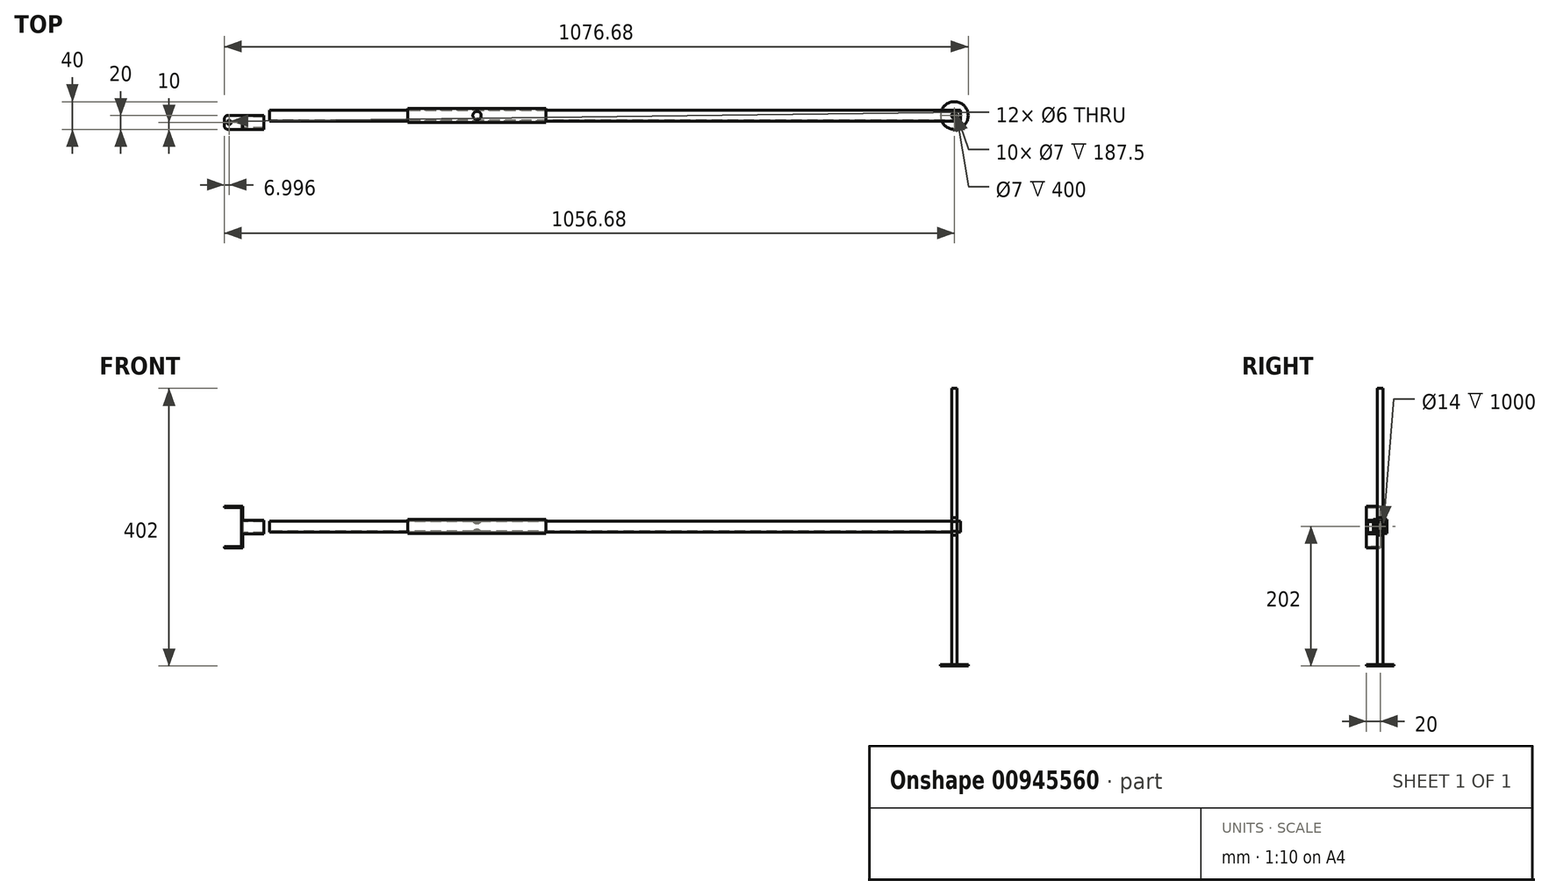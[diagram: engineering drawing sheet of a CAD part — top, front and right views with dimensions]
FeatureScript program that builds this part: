
annotation { "Feature Type Name" : "Feature", "Feature Type Description" : "" }
export const myFeature = defineFeature(function(context is Context, id is Id, definition is map)
    precondition{}
    {
        {
            var Q0;
            Q0=qCreatedBy(makeId("Right.planeOp"),FACE);
            var sketch = newSketch(context, id + "F0", { "sketchPlane" : qUnion([Q0])});
            skLineSegment(sketch, "E0.bottom", {"start": v(10, 10) * mm, "end": v(-10, 10) * mm});
            skLineSegment(sketch, "E0.top", {"start": v(10, -10) * mm, "end": v(-10, -10) * mm});
            skLineSegment(sketch, "E0.left", {"start": v(10, 10) * mm, "end": v(10, -10) * mm});
            skLineSegment(sketch, "E0.right", {"start": v(-10, 10) * mm, "end": v(-10, -10) * mm});
            skPoint(sketch, "E0.middle", {"position": v(0, 0) * mm});
            skLineSegment(sketch, "E1.0", {"start": v(8, 8) * mm, "end": v(-8, 8) * mm});
            skLineSegment(sketch, "E1.1", {"start": v(8, 8) * mm, "end": v(8, -8) * mm});
            skLineSegment(sketch, "E1.2", {"start": v(8, -8) * mm, "end": v(-8, -8) * mm});
            skLineSegment(sketch, "E1.3", {"start": v(-8, 8) * mm, "end": v(-8, -8) * mm});
            skSolve(sketch);
        }
        {
            var Q0;
            Q0=makeQuery(id+"F0.imprint","IMPRINT",FACE,{"disambiguationData":[TD([[makeQuery(id+"F0.imprint","IMPRINT",EDGE,{"derivedFrom":sQuery(id+"F0.wireOp",EDGE,"E0.bottom")}),1.0]])]});
            extrude(context, id + "F1", {"entities" : qUnion([Q0]), "depth" : 200 * mm, "offsetDistance" : 25 * mm});
        }
        {
            var Q0;
            Q0=qCreatedBy(makeId("Right.planeOp"),FACE);
            var sketch = newSketch(context, id + "F2", { "sketchPlane" : qUnion([Q0])});
            skCircle(sketch, "E2", {"center": v(0, 0) * mm, "radius": 8 * mm});
            skCircle(sketch, "E3", {"center": v(0, 0) * mm, "radius": 7 * mm});
            skSolve(sketch);
        }
        {
            var Q0;
            Q0=makeQuery(id+"F2.imprint","IMPRINT",FACE,{"disambiguationData":[TD([[makeQuery(id+"F2.imprint","IMPRINT",EDGE,{"derivedFrom":sQuery(id+"F2.wireOp",EDGE,"E2")}),1.0]])]});
            extrude(context, id + "F3", {"entities" : qUnion([Q0]), "operationType" : NewBodyOperationType.ADD, "depth" : 800 * mm, "offsetDistance" : 25 * mm, "hasSecondDirection" : true, "secondDirectionOppositeDirection" : true, "secondDirectionDepth" : 200 * mm});
        }
        {
            var Q0;
            Q0=makeQuery(id+"F1.opExtrude","SWEPT_FACE",FACE,{"disambiguationData":[OSD([sQuery(id+"F0.wireOp",EDGE,"E0.top")])]});
            var sketch = newSketch(context, id + "F4", { "sketchPlane" : qUnion([Q0])});
            skCircle(sketch, "E4", {"center": v(100, 0) * mm, "radius": 6 * mm});
            skLineSegment(sketch, "E5", {"start": v(0, 0) * mm, "end": v(200, 0) * mm, "construction": true});
            skSolve(sketch);
        }
        {
            var Q0;
            Q0=makeQuery(id+"F4.imprint","IMPRINT",FACE,{"disambiguationData":[TD([[makeQuery(id+"F4.imprint","IMPRINT",EDGE,{"derivedFrom":sQuery(id+"F4.wireOp",EDGE,"E4")}),1.0]])]});
            extrude(context, id + "F5", {"entities" : qUnion([Q0]), "operationType" : NewBodyOperationType.REMOVE, "oppositeDirection" : true, "depth" : 25 * mm, "offsetDistance" : 25 * mm});
        }
        {
            var Q0;
            Q0=qCreatedBy(makeId("Top.planeOp"),FACE);
            var sketch = newSketch(context, id + "F6", { "sketchPlane" : qUnion([Q0])});
            skCircle(sketch, "E6", {"center": v(791, 0) * mm, "radius": 4 * mm});
            skSolve(sketch);
        }
        {
            var Q0;
            Q0 = qSketchRegion(id + "F6", true);
            extrude(context, id + "F7", {"entities" : qUnion([Q0]), "operationType" : NewBodyOperationType.REMOVE, "endBound" : BoundingType.SYMMETRIC, "oppositeDirection" : true, "depth" : 25 * mm, "offsetDistance" : 25 * mm});
        }
        {
            var Q0;
            Q0 = qSketchRegion(id + "F6", true);
            extrude(context, id + "F8", {"entities" : qUnion([Q0]), "endBound" : BoundingType.SYMMETRIC, "depth" : 400 * mm, "offsetDistance" : 25 * mm});
        }
        {
            var Q0;
            Q0=makeQuery(id+"F8.opExtrude","CAP_FACE",FACE,{"disambiguationData":[OSD([sQuery(id+"F6.wireOp",EDGE,"E6")])],"isStart":false});
            var Q1;
            Q1=makeQuery(id+"F8.opExtrude","CAP_FACE",FACE,{"disambiguationData":[OSD([sQuery(id+"F6.wireOp",EDGE,"E6")])],"isStart":true});
            shell(context, id + "F9", {"entities" : qUnion([Q0, Q1]), "thickness" : 0.5 * mm});
        }
        {
            var Q0;
            Q0=makeQuery(id+"F8.opExtrude","CAP_FACE",FACE,{"disambiguationData":[OSD([sQuery(id+"F6.wireOp",EDGE,"E6")])],"isStart":true});
            var sketch = newSketch(context, id + "F10", { "sketchPlane" : qUnion([Q0])});
            skCircle(sketch, "E7", {"center": v(791, 0) * mm, "radius": 20 * mm});
            skSolve(sketch);
        }
        {
            var Q0;
            Q0 = qSketchRegion(id + "F10", true);
            extrude(context, id + "F11", {"entities" : qUnion([Q0]), "depth" : 2 * mm, "offsetDistance" : 25 * mm});
        }
        {
            var Q0;
            Q0=qCreatedBy(makeId("Front.planeOp"),FACE);
            var sketch = newSketch(context, id + "F12", { "sketchPlane" : qUnion([Q0])});
            skLineSegment(sketch, "E8", {"start": v(-208.68, -11) * mm, "end": v(-208.68, 9) * mm});
            skLineSegment(sketch, "E9", {"start": v(-208.68, 9) * mm, "end": v(-238.68, 9) * mm});
            skLineSegment(sketch, "E10", {"start": v(-238.68, 9) * mm, "end": v(-238.68, 29.24) * mm});
            skLineSegment(sketch, "E11", {"start": v(-238.68, 29.24) * mm, "end": v(-265.68, 29.24) * mm});
            skLineSegment(sketch, "E12", {"start": v(-265.68, 29.24) * mm, "end": v(-265.68, 27.24) * mm});
            skLineSegment(sketch, "E13", {"start": v(-265.68, 27.24) * mm, "end": v(-240.68, 27.24) * mm});
            skLineSegment(sketch, "E14", {"start": v(-240.68, 27.24) * mm, "end": v(-240.68, -29.26) * mm});
            skLineSegment(sketch, "E15", {"start": v(-240.68, -29.26) * mm, "end": v(-265.68, -29.26) * mm});
            skLineSegment(sketch, "E16", {"start": v(-265.68, -29.26) * mm, "end": v(-265.68, -31.26) * mm});
            skLineSegment(sketch, "E17", {"start": v(-208.68, -11) * mm, "end": v(-208.68, -11) * mm});
            skLineSegment(sketch, "E18", {"start": v(-208.68, -11) * mm, "end": v(-238.68, -11) * mm});
            skLineSegment(sketch, "E19", {"start": v(-238.68, -11) * mm, "end": v(-238.68, -31.26) * mm});
            skLineSegment(sketch, "E20", {"start": v(-238.68, -31.26) * mm, "end": v(-265.68, -31.26) * mm});
            skSolve(sketch);
        }
        {
            var Q0;
            Q0 = qSketchRegion(id + "F12", true);
            extrude(context, id + "F13", {"entities" : qUnion([Q0]), "depth" : 20 * mm, "offsetDistance" : 25 * mm});
        }
        {
            var Q0;
            Q0=makeQuery(id+"F13.opExtrude","SWEPT_FACE",FACE,{"disambiguationData":[OSD([sQuery(id+"F12.wireOp",EDGE,"E8")])]});
            shell(context, id + "F14", {"entities" : qUnion([Q0]), "thickness" : 2 * mm});
        }
        {
            var Q0;
            Q0=makeQuery(id+"F13.opExtrude","SWEPT_FACE",FACE,{"disambiguationData":[OSD([sQuery(id+"F12.wireOp",EDGE,"E11")])]});
            var sketch = newSketch(context, id + "F15", { "sketchPlane" : qUnion([Q0])});
            skCircle(sketch, "E21", {"center": v(-258.68, -10) * mm, "radius": 3 * mm});
            skLineSegment(sketch, "E22", {"start": v(-258.68, -10) * mm, "end": v(-238.68, -10) * mm, "construction": true});
            skSolve(sketch);
        }
        {
            var Q0;
            Q0 = qSketchRegion(id + "F15", true);
            extrude(context, id + "F16", {"entities" : qUnion([Q0]), "operationType" : NewBodyOperationType.REMOVE, "endBound" : BoundingType.THROUGH_ALL, "oppositeDirection" : true, "depth" : 25 * mm, "offsetDistance" : 25 * mm});
        }
        {
            var Q0;
            Q0=makeQuery(id+"F13.opExtrude","CAP_EDGE",EDGE,{"disambiguationData":[OSD([sQuery(id+"F12.wireOp",EDGE,"E12")])],"isStart":false});
            var Q1;
            Q1=makeQuery(id+"F13.opExtrude","CAP_EDGE",EDGE,{"disambiguationData":[OSD([sQuery(id+"F12.wireOp",EDGE,"E12")])],"isStart":true});
            var Q2;
            Q2=makeQuery(id+"F13.opExtrude","CAP_EDGE",EDGE,{"disambiguationData":[OSD([sQuery(id+"F12.wireOp",EDGE,"E16")])],"isStart":false});
            var Q3;
            Q3=makeQuery(id+"F13.opExtrude","CAP_EDGE",EDGE,{"disambiguationData":[OSD([sQuery(id+"F12.wireOp",EDGE,"E16")])],"isStart":true});
            fillet(context, id + "F17", {"entities" : qUnion([Q0, Q1, Q2, Q3]), "radius" : 5 * mm, "tangentPropagation" : true, "allowEdgeOverflow" : false});
        }
    });
